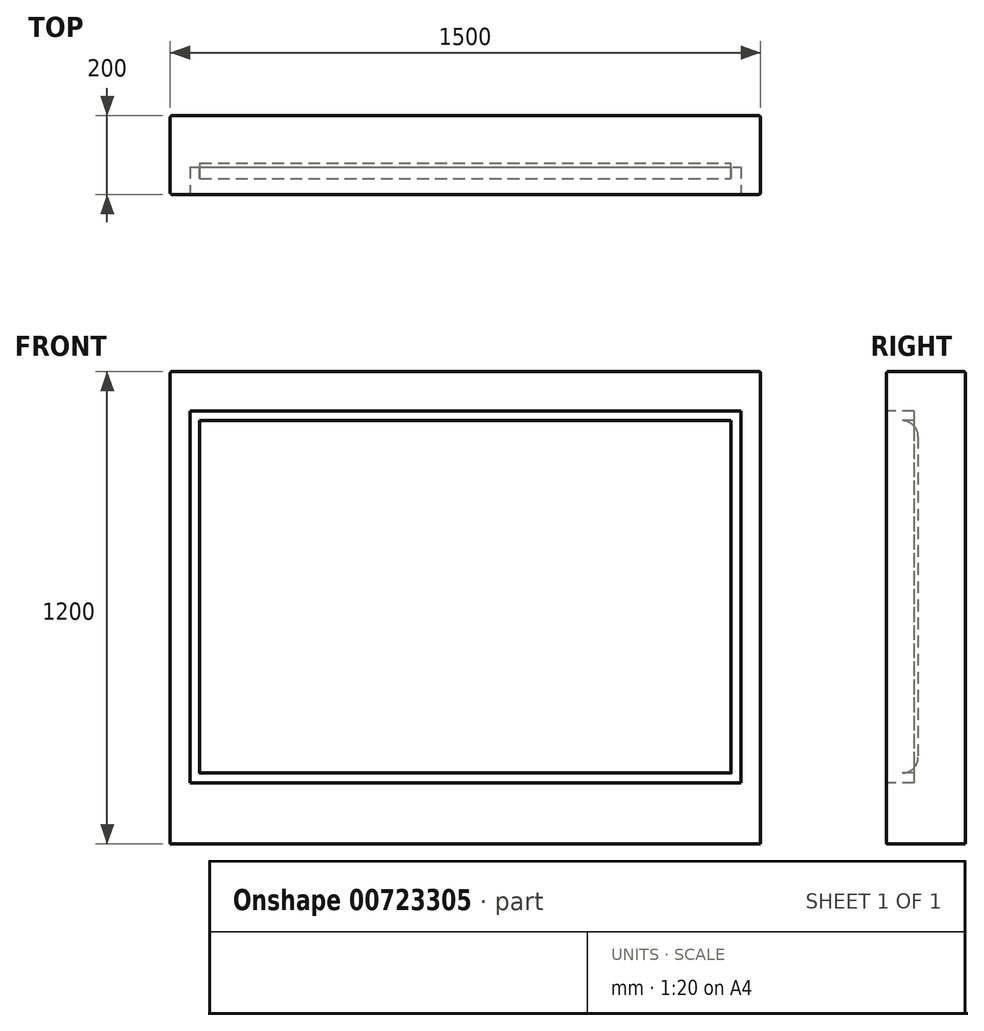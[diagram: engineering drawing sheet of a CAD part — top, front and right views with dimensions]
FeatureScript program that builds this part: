
annotation { "Feature Type Name" : "Feature", "Feature Type Description" : "" }
export const myFeature = defineFeature(function(context is Context, id is Id, definition is map)
    precondition{}
    {
        {
            var Q0;
            Q0=qCreatedBy(makeId("Front.planeOp"),FACE);
            var sketch = newSketch(context, id + "F0", { "sketchPlane" : qUnion([Q0])});
            skLineSegment(sketch, "E0.bottom", {"start": v(0, 0) * mm, "end": v(-1500, 0) * mm});
            skLineSegment(sketch, "E0.top", {"start": v(0, 1200) * mm, "end": v(-1500, 1200) * mm});
            skLineSegment(sketch, "E0.left", {"start": v(0, 0) * mm, "end": v(0, 1200) * mm});
            skLineSegment(sketch, "E0.right", {"start": v(-1500, 0) * mm, "end": v(-1500, 1200) * mm});
            skSolve(sketch);
        }
        {
            var Q0;
            Q0 = qSketchRegion(id + "F0", true);
            extrude(context, id + "F1", {"entities" : qUnion([Q0]), "depth" : 200 * mm, "offsetDistance" : 25 * mm});
        }
        {
            var Q0;
            Q0=makeQuery(id+"F1.opExtrude","SWEPT_EDGE",EDGE,{"disambiguationData":[OSD([sQuery(id+"F0.wireOp",EDGE,"E0.top"),sQuery(id+"F0.wireOp",EDGE,"E0.right")])]});
            var Q1;
            Q1=makeQuery(id+"F1.opExtrude","SWEPT_EDGE",EDGE,{"disambiguationData":[OSD([sQuery(id+"F0.wireOp",EDGE,"E0.top"),sQuery(id+"F0.wireOp",EDGE,"E0.left")])]});
            var Q2;
            Q2=makeQuery(id+"F1.opExtrude","CAP_EDGE",EDGE,{"disambiguationData":[OSD([sQuery(id+"F0.wireOp",EDGE,"E0.top")])],"isStart":true});
            var Q3;
            Q3=makeQuery(id+"F1.opExtrude","CAP_EDGE",EDGE,{"disambiguationData":[OSD([sQuery(id+"F0.wireOp",EDGE,"E0.top")])],"isStart":false});
            var Q4;
            Q4=makeQuery(id+"F1.opExtrude","CAP_EDGE",EDGE,{"disambiguationData":[OSD([sQuery(id+"F0.wireOp",EDGE,"E0.right")])],"isStart":false});
            var Q5;
            Q5=makeQuery(id+"F1.opExtrude","CAP_EDGE",EDGE,{"disambiguationData":[OSD([sQuery(id+"F0.wireOp",EDGE,"E0.right")])],"isStart":true});
            var Q6;
            Q6=makeQuery(id+"F1.opExtrude","CAP_EDGE",EDGE,{"disambiguationData":[OSD([sQuery(id+"F0.wireOp",EDGE,"E0.left")])],"isStart":false});
            var Q7;
            Q7=makeQuery(id+"F1.opExtrude","CAP_EDGE",EDGE,{"disambiguationData":[OSD([sQuery(id+"F0.wireOp",EDGE,"E0.left")])],"isStart":true});
            fillet(context, id + "F2", {"entities" : qUnion([Q0, Q1, Q2, Q3, Q4, Q5, Q6, Q7]), "radius" : 5 * mm, "tangentPropagation" : true, "allowEdgeOverflow" : false});
        }
        {
            var Q0;
            Q0=makeQuery(id+"F1.opExtrude","CAP_FACE",FACE,{"disambiguationData":[OSD([sQuery(id+"F0.wireOp",EDGE,"E0.bottom"),sQuery(id+"F0.wireOp",EDGE,"E0.top"),sQuery(id+"F0.wireOp",EDGE,"E0.left"),sQuery(id+"F0.wireOp",EDGE,"E0.right")])],"isStart":false});
            var sketch = newSketch(context, id + "F3", { "sketchPlane" : qUnion([Q0])});
            skLineSegment(sketch, "E1.0.0", {"start": v(-5, 1195) * mm, "end": v(-1495, 1195) * mm});
            skLineSegment(sketch, "E1.0.1", {"start": v(-1495, 1195) * mm, "end": v(-1495, 0) * mm});
            skLineSegment(sketch, "E1.0.2", {"start": v(-1495, 0) * mm, "end": v(-5, 0) * mm});
            skLineSegment(sketch, "E1.0.3", {"start": v(-5, 0) * mm, "end": v(-5, 1195) * mm});
            skLineSegment(sketch, "E2.bottom", {"start": v(-1425, 1075) * mm, "end": v(-75, 1075) * mm});
            skLineSegment(sketch, "E2.top", {"start": v(-1425, 180) * mm, "end": v(-75, 180) * mm});
            skLineSegment(sketch, "E2.left", {"start": v(-1425, 1075) * mm, "end": v(-1425, 180) * mm});
            skLineSegment(sketch, "E2.right", {"start": v(-75, 1075) * mm, "end": v(-75, 180) * mm});
            skSolve(sketch);
        }
        {
            var Q0;
            Q0=makeQuery(id+"F3.imprint","IMPRINT",FACE,{"disambiguationData":[TD([[makeQuery(id+"F3.imprint","IMPRINT",EDGE,{"derivedFrom":sQuery(id+"F3.wireOp",EDGE,"E2.bottom")}),-1.0]])]});
            extrude(context, id + "F4", {"entities" : qUnion([Q0]), "operationType" : NewBodyOperationType.REMOVE, "oppositeDirection" : true, "depth" : 80 * mm, "offsetDistance" : 25 * mm});
        }
        {
            var Q0;
            Q0=makeQuery(id+"F4.boolean.opBoolean","COPY",EDGE,{"derivedFrom":makeQuery(id+"F4.opExtrude","CAP_EDGE",EDGE,{"disambiguationData":[OSD([sQuery(id+"F3.wireOp",EDGE,"E2.top")])],"isStart":false})});
            var Q1;
            Q1=makeQuery(id+"F4.boolean.opBoolean","COPY",EDGE,{"derivedFrom":makeQuery(id+"F4.opExtrude","CAP_EDGE",EDGE,{"disambiguationData":[OSD([sQuery(id+"F3.wireOp",EDGE,"E2.bottom")])],"isStart":false})});
            fillet(context, id + "F5", {"entities" : qUnion([Q0, Q1]), "radius" : 40 * mm, "tangentPropagation" : true, "allowEdgeOverflow" : false});
        }
        {
            var Q0;
            Q0=makeQuery(id+"F1.opExtrude","CAP_FACE",FACE,{"disambiguationData":[OSD([sQuery(id+"F0.wireOp",EDGE,"E0.bottom"),sQuery(id+"F0.wireOp",EDGE,"E0.top"),sQuery(id+"F0.wireOp",EDGE,"E0.left"),sQuery(id+"F0.wireOp",EDGE,"E0.right")])],"isStart":false});
            var sketch = newSketch(context, id + "F6", { "sketchPlane" : qUnion([Q0])});
            skLineSegment(sketch, "E3.0", {"start": v(-1425, 1075) * mm, "end": v(-75, 1075) * mm});
            skLineSegment(sketch, "E4.0", {"start": v(-1425, 1075) * mm, "end": v(-1425, 180) * mm});
            skLineSegment(sketch, "E5.0", {"start": v(-75, 1075) * mm, "end": v(-75, 180) * mm});
            skLineSegment(sketch, "E6.0", {"start": v(-1425, 180) * mm, "end": v(-75, 180) * mm});
            skLineSegment(sketch, "E7.bottom", {"start": v(-1450, 1100) * mm, "end": v(-50, 1100) * mm});
            skLineSegment(sketch, "E7.top", {"start": v(-1450, 155) * mm, "end": v(-50, 155) * mm});
            skLineSegment(sketch, "E7.left", {"start": v(-1450, 1100) * mm, "end": v(-1450, 155) * mm});
            skLineSegment(sketch, "E7.right", {"start": v(-50, 1100) * mm, "end": v(-50, 155) * mm});
            skSolve(sketch);
        }
        {
            var Q0;
            Q0 = qSketchRegion(id + "F6", true);
            extrude(context, id + "F7", {"entities" : qUnion([Q0]), "operationType" : NewBodyOperationType.REMOVE, "oppositeDirection" : true, "depth" : 70 * mm, "offsetDistance" : 25 * mm});
        }
    });
